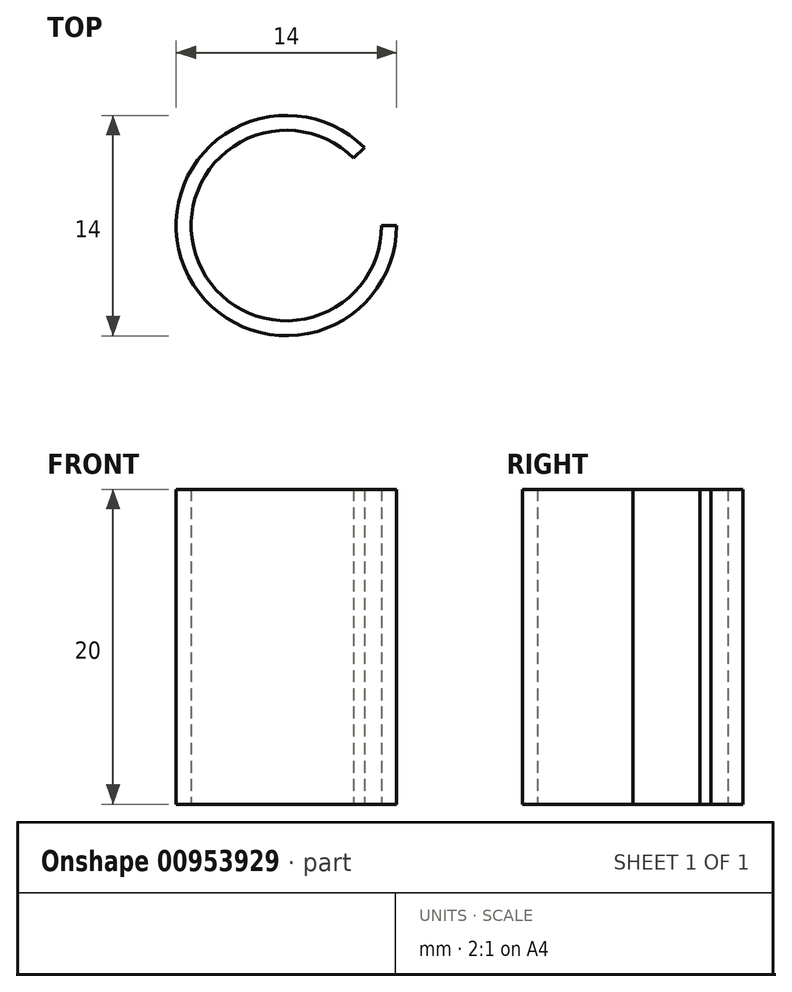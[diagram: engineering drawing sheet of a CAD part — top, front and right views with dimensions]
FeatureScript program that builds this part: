
annotation { "Feature Type Name" : "Feature", "Feature Type Description" : "" }
export const myFeature = defineFeature(function(context is Context, id is Id, definition is map)
    precondition{}
    {
        {
            var Q0;
            Q0=qCreatedBy(makeId("Top.planeOp"),FACE);
            var sketch = newSketch(context, id + "F0", { "sketchPlane" : qUnion([Q0])});
            skCircle(sketch, "E0", {"center": v(0, 0) * mm, "radius": 7 * mm});
            skCircle(sketch, "E1", {"center": v(0, 0) * mm, "radius": 6.05 * mm});
            skLineSegment(sketch, "E2", {"start": v(0, 6.05) * mm, "end": v(0, 7) * mm});
            skLineSegment(sketch, "E3", {"start": v(6.05, 0) * mm, "end": v(7, 0) * mm});
            skLineSegment(sketch, "E4", {"start": v(7, 0) * mm, "end": v(7, 10.7) * mm, "construction": true});
            skLineSegment(sketch, "E5", {"start": v(0, 7) * mm, "end": v(12.14, 7) * mm, "construction": true});
            skLineSegment(sketch, "E6", {"start": v(0, 0) * mm, "end": v(7, 7) * mm});
            skSolve(sketch);
        }
        {
            var Q0;
            {var subQ0=sQuery(id+"F0.wireOp",EDGE,"E2");Q0=makeQuery(id+"F0.imprint","IMPRINT",FACE,{"disambiguationData":[TD([[makeQuery(id+"F0.imprint","IMPRINT",EDGE,{"derivedFrom":subQ0}),-1.0]])]});}
            var Q1;
            {var subQ0=sQuery(id+"F0.wireOp",EDGE,"E2");Q1=makeQuery(id+"F0.imprint","IMPRINT",FACE,{"disambiguationData":[TD([[makeQuery(id+"F0.imprint","IMPRINT",EDGE,{"derivedFrom":subQ0}),1.0]])]});}
            extrude(context, id + "F1", {"entities" : qUnion([Q0, Q1]), "depth" : 20 * mm, "offsetDistance" : 25 * mm});
        }
    });
